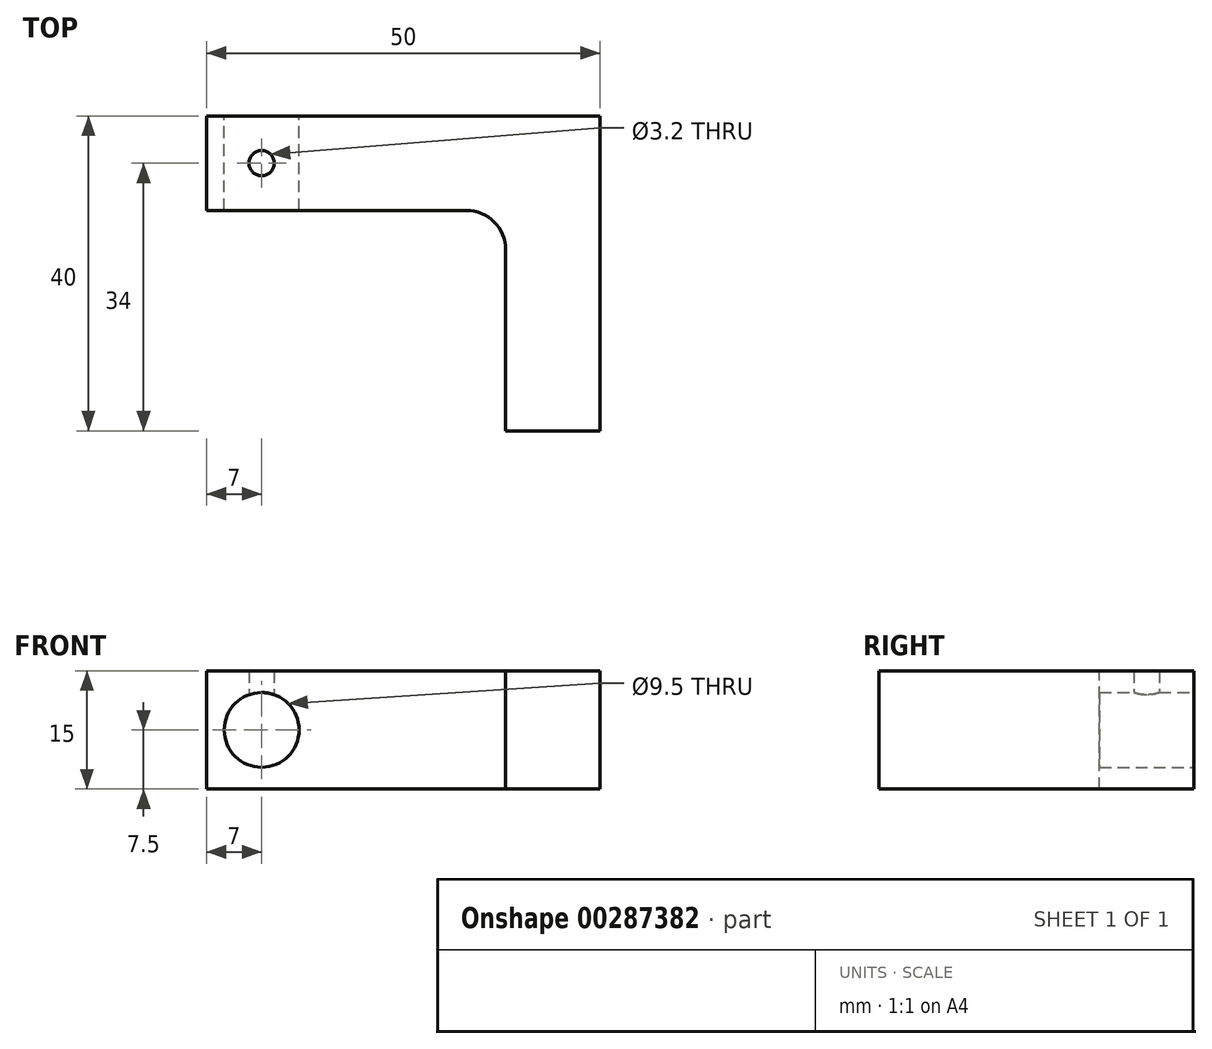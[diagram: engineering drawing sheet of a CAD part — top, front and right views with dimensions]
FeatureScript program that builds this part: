
annotation { "Feature Type Name" : "Feature", "Feature Type Description" : "" }
export const myFeature = defineFeature(function(context is Context, id is Id, definition is map)
    precondition{}
    {
        {
            var Q0;
            Q0=qCreatedBy(makeId("Top.planeOp"),FACE);
            var sketch = newSketch(context, id + "F0", { "sketchPlane" : qUnion([Q0])});
            skLineSegment(sketch, "E0", {"start": v(0, 0) * mm, "end": v(-38, 0) * mm});
            skLineSegment(sketch, "E1", {"start": v(-38, 0) * mm, "end": v(-38, 12) * mm});
            skLineSegment(sketch, "E2", {"start": v(-38, 12) * mm, "end": v(12, 12) * mm});
            skLineSegment(sketch, "E3", {"start": v(12, 12) * mm, "end": v(12, -28) * mm});
            skLineSegment(sketch, "E4", {"start": v(12, -28) * mm, "end": v(0, -28) * mm});
            skLineSegment(sketch, "E5", {"start": v(0, -28) * mm, "end": v(0, 0) * mm});
            skSolve(sketch);
        }
        {
            var Q0;
            Q0=qSketchRegion(id+"F0",true);
            extrude(context, id + "F1", {"entities" : qUnion([Q0]), "oppositeDirection" : true, "depth" : 15 * mm});
        }
        {
            var Q0;
            Q0=makeQuery(id+"F1.opExtrude","SWEPT_FACE",FACE,{"disambiguationData":[OSD([sQuery(id+"F0.wireOp",EDGE,"E0")])]});
            var sketch = newSketch(context, id + "F2", { "sketchPlane" : qUnion([Q0])});
            skPoint(sketch, "E6", {"position": v(-31, -7.5) * mm});
            skPoint(sketch, "E6.positionSnap0", {"position": v(-38, -7.5) * mm});
            skSolve(sketch);
        }
        {
            var Q0;
            Q0=sQuery(id+"F2.wireOp",VERTEX,"E6");
            var Q1;
            Q1=makeQuery(id+"F1.opExtrude","SWEPT_BODY",BODY,{"disambiguationData":[OSD([sQuery(id+"F0.wireOp",EDGE,"E0"),sQuery(id+"F0.wireOp",EDGE,"E1"),sQuery(id+"F0.wireOp",EDGE,"E2"),sQuery(id+"F0.wireOp",EDGE,"E3"),sQuery(id+"F0.wireOp",EDGE,"E4"),sQuery(id+"F0.wireOp",EDGE,"E5")])]});
            hole(context, id + "F3", {"style" : HoleStyle.SIMPLE, "endStyle" : HoleEndStyle.THROUGH, "standardTappedOrClearance" : lookupTablePath({ "standard" : "ISO", "size" : "9.5", "type" : "Drilled" }), "standardBlindInLast" : lookupTablePath({ "standard" : "ISO", "size" : "9.5", "type" : "Drilled" }), "holeDiameter" : 9.5 * mm, "tappedDepth" : 6 * mm, "tapClearance" : 2, "locations" : qUnion([Q0]), "scope" : qUnion([Q1])});
        }
        {
            var Q0;
            Q0=makeQuery(id+"F1.opExtrude","CAP_FACE",FACE,{"disambiguationData":[OSD([sQuery(id+"F0.wireOp",EDGE,"E0"),sQuery(id+"F0.wireOp",EDGE,"E1"),sQuery(id+"F0.wireOp",EDGE,"E2"),sQuery(id+"F0.wireOp",EDGE,"E3"),sQuery(id+"F0.wireOp",EDGE,"E4"),sQuery(id+"F0.wireOp",EDGE,"E5")])],"isStart":true});
            var sketch = newSketch(context, id + "F4", { "sketchPlane" : qUnion([Q0])});
            skPoint(sketch, "E7", {"position": v(-31, 6) * mm});
            skSolve(sketch);
        }
        {
            var Q0;
            Q0=sQuery(id+"F4.wireOp",VERTEX,"E7");
            var Q1;
            Q1=makeQuery(id+"F1.opExtrude","SWEPT_BODY",BODY,{"disambiguationData":[OSD([sQuery(id+"F0.wireOp",EDGE,"E0"),sQuery(id+"F0.wireOp",EDGE,"E1"),sQuery(id+"F0.wireOp",EDGE,"E2"),sQuery(id+"F0.wireOp",EDGE,"E3"),sQuery(id+"F0.wireOp",EDGE,"E4"),sQuery(id+"F0.wireOp",EDGE,"E5")])]});
            hole(context, id + "F5", {"style" : HoleStyle.SIMPLE, "endStyle" : HoleEndStyle.BLIND, "standardTappedOrClearance" : lookupTablePath({ "standard" : "ISO", "engagement" : "75%", "pitch" : "0.75 mm", "size" : "M4", "type" : "Tapped" }), "standardBlindInLast" : lookupTablePath({ "standard" : "ISO", "engagement" : "75%", "pitch" : "0.75 mm", "size" : "M4", "type" : "Tapped" }), "holeDiameter" : 3.2 * mm, "showTappedDepth" : true, "holeDepth" : 7.5 * mm, "tappedDepth" : 6 * mm, "tapClearance" : 2, "locations" : qUnion([Q0]), "scope" : qUnion([Q1])});
        }
        {
            var Q0;
            Q0=makeQuery(id+"F1.opExtrude","SWEPT_EDGE",EDGE,{"disambiguationData":[OSD([sQuery(id+"F0.wireOp",EDGE,"E0"),sQuery(id+"F0.wireOp",EDGE,"E5")])]});
            fillet(context, id + "F6", {"entities" : qUnion([Q0]), "radius" : 5 * mm, "tangentPropagation" : true, "allowEdgeOverflow" : false});
        }
    });
